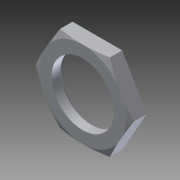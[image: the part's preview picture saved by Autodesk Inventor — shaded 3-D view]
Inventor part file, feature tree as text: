
AUTODESK INVENTOR PART (.ipt)
format: ipt  version: 2011 SP1 (Build 150282100, 282)  size: 108,544 bytes
history: native  units: in
note: dims shown in document units (in); Inventor stores cm internally (conversion verified against a paired STEP export)
features: other x7, sketch x3, revolve x1, extrude x1, hole x1
ambient origin geometry x8: Origin, YZ Plane, XZ Plane, XY Plane, X Axis, Y Axis, Z Axis, Center Point
bodies: Solid1 (feature_tree)
feature tree (13):
  revolve  "Revolution1"  [1 undecoded]
  extrude  "Extrusion1"  [1 undecoded]
  hole  "Drilling 1"  [1 undecoded]
  other  "nut_XY"
  other  "nut_YZ"
  other  "nut_ZX"
  other  "nut_X"
  other  "nut_Y"
  other  "nut_Z"
  other  "nut_Center"
  sketch  "Sketch_1"  dims[d0=360.0deg d1=0.188in d2=0.0in]
  sketch  "Sketch_2"  dims[d3=0.3979in d4=0.75in d5=0.472in d6=0.25in d7=0.6184in d8=0.094in d9=0.0in]
  sketch  "Sketch3"
note: 3 required parameter values undecoded (feature->parameter linkage not recoverable at this tier; creation-order binding heuristic only, values carry confidence <= 0.55)